# Revit family: DCST_Счетчик водяной комбинированный_СТВК 2
name_source: partatom
category: Арматура трубопроводов
units: mm (PartAtom-declared; Revit-internal decimal feet)

## family parameters
Всегда вертикально = Да
На основе рабочей плоскости = Нет
Общий = Нет
При загрузке вырезать с полостями = Нет
Размер круглого соединителя = Использовать диаметр
Тип детали = Вставляется

## types (5) — shared parameters
ADSK_Единица измерения = шт.
ADSK_Завод-изготовитель = Декаст
ADSK_Количество = 1
ADSK_Материал = Декаст_Корпус счетчика темно-синий
LT = СТВК 2
URL = https://www.decast.com
ИПД_ДГ2 = ♦ : импульсный выход (геркон)
ИПД_Нет = ♦ : нет
Изготовитель = Декаст

## per-type parameters (varying)
- СТВК 2 50/15: ADSK_Диаметр условный=50 мм; CS1=114 мм; CS2=26 мм; D1=60 мм; D2=120 мм; D22=140 мм; D3=68 мм; D4=60 мм; D5=24 мм; L=190 мм; S=76 мм; T=103 мм; W1=133 мм; W2=128 мм; f=13 мм; h1=72 мм; h2=38.5 мм; h3=12.7 мм; h4=15 мм; ws1=72 мм; ws2=37 мм; Диаметр малого счетчика=15 мм; Диаметр условного прохода=50 мм; Монтажная длина=280 мм; УГО_Высота=127 мм; УГО_Длина=254 мм; УГО_Длина линии=13 мм
- СТВК 2 80/20: ADSK_Диаметр условный=80 мм; CS1=147 мм; CS2=32 мм; D1=92 мм; D2=126 мм; D22=146 мм; D3=94 мм; D4=94 мм; D5=32 мм; L=225 мм; S=80.3 мм; T=112.5 мм; W1=162 мм; W2=136 мм; f=16 мм; h1=76 мм; h2=44 мм; h3=15.4 мм; h4=18 мм; ws1=92.5 мм; ws2=45 мм; Диаметр малого счетчика=20 мм; Диаметр условного прохода=80 мм; Монтажная длина=370 мм; УГО_Высота=169 мм; УГО_Длина=338 мм; УГО_Длина линии=16 мм
- СТВК 2 100/25: ADSK_Диаметр условный=100 мм; CS1=158 мм; CS2=29 мм; D1=110 мм; D2=126 мм; D22=146 мм; D3=124 мм; D4=124 мм; D5=27.5 мм; L=225 мм; S=91.3 мм; T=112.5 мм; W1=162 мм; W2=136 мм; f=16 мм; h1=76 мм; h2=50 мм; h3=15.4 мм; h4=18 мм; ws1=82 мм; ws2=45 мм; Диаметр малого счетчика=25 мм; Диаметр условного прохода=100 мм; Монтажная длина=370 мм; УГО_Высота=169 мм; УГО_Длина=338 мм; УГО_Длина линии=16 мм
- СТВК 2 150/40: ADSK_Диаметр условный=150 мм; CS1=222.4 мм; CS2=43 мм; D1=160 мм; D2=195 мм; D22=215 мм; D3=168 мм; D4=161 мм; D5=41 мм; L=300 мм; S=151.9 мм; T=170.5 мм; W1=265.5 мм; W2=215 мм; f=22 мм; h1=86 мм; h2=96 мм; h3=21 мм; h4=21 мм; ws1=133 мм; ws2=55 мм; Диаметр малого счетчика=40 мм; Диаметр условного прохода=150 мм; Монтажная длина=500 мм; УГО_Высота=228 мм; УГО_Длина=456 мм; УГО_Длина линии=22 мм
- СТВК 2 65/20: ADSK_Диаметр условный=65 мм; CS1=142 мм; CS2=32 мм; D1=92 мм; D2=120 мм; D22=140 мм; D3=80 мм; D4=80 мм; D5=32 мм; L=190 мм; S=80.3 мм; T=103 мм; W1=133 мм; W2=128 мм; f=13 мм; h1=72 мм; h2=38.5 мм; h3=12.7 мм; h4=15 мм; ws1=72 мм; ws2=37 мм; Диаметр малого счетчика=20 мм; Диаметр условного прохода=65 мм; Монтажная длина=370 мм; УГО_Высота=172 мм; УГО_Длина=344 мм; УГО_Длина линии=13 мм
